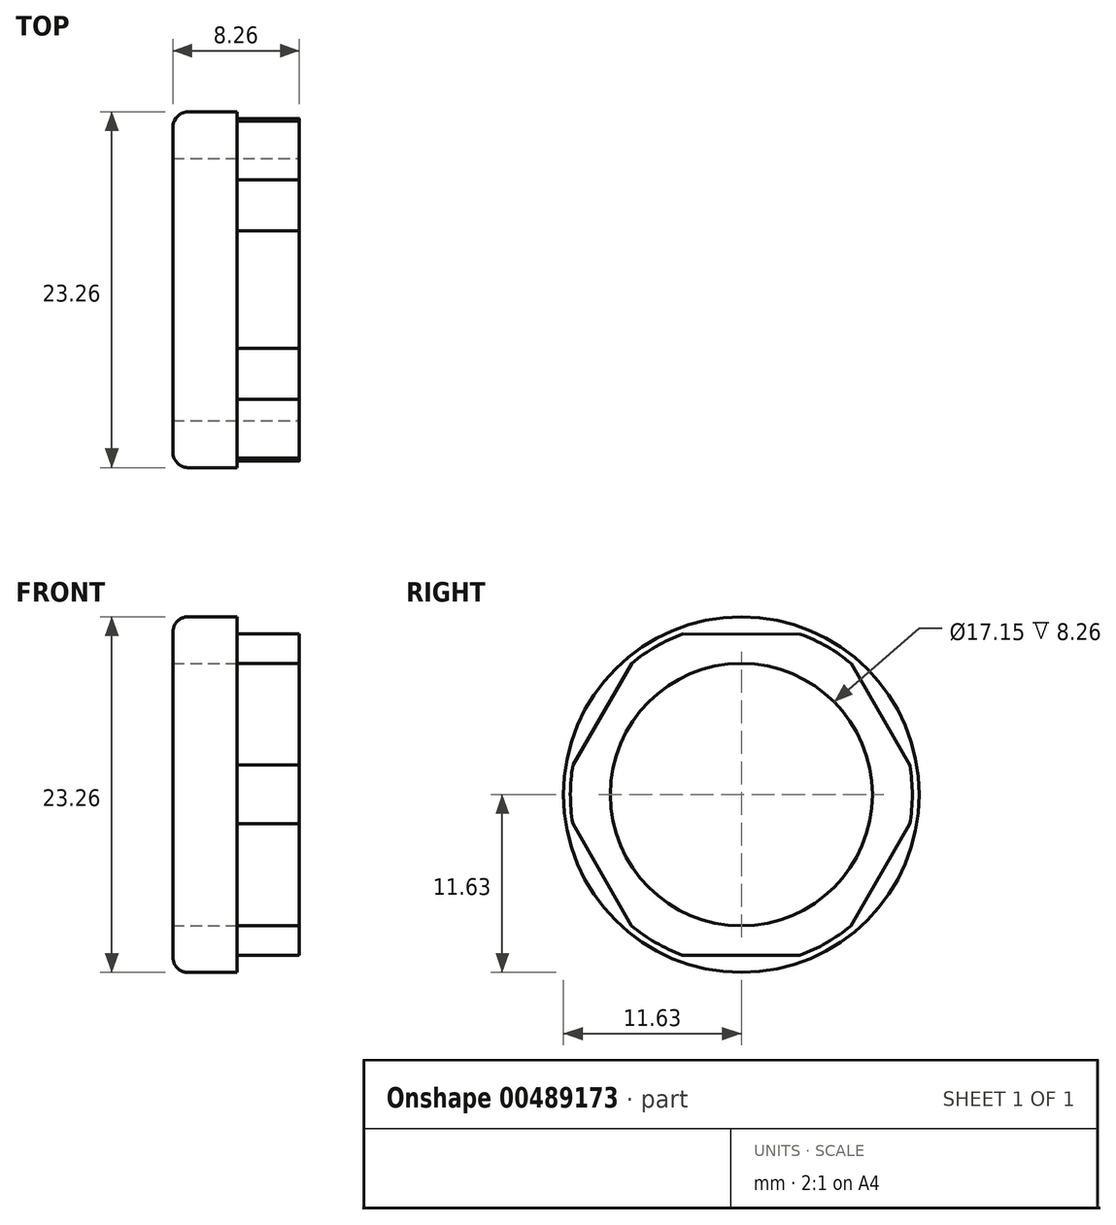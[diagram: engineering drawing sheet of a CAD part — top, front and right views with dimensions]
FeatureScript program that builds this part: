
annotation { "Feature Type Name" : "Feature", "Feature Type Description" : "" }
export const myFeature = defineFeature(function(context is Context, id is Id, definition is map)
    precondition{}
    {
        {
            var Q0;
            Q0=qCreatedBy(makeId("Front.planeOp"),FACE);
            var sketch = newSketch(context, id + "F0", { "sketchPlane" : qUnion([Q0])});
            skLineSegment(sketch, "E0", {"start": v(4.06, 8.57) * mm, "end": v(-4.2, 8.57) * mm});
            skLineSegment(sketch, "E1", {"start": v(-4.2, 8.57) * mm, "end": v(-4.2, 11.63) * mm});
            skLineSegment(sketch, "E2", {"start": v(-4.2, 11.63) * mm, "end": v(0, 11.63) * mm});
            skLineSegment(sketch, "E3", {"start": v(0, 11.63) * mm, "end": v(0, 11.18) * mm});
            skLineSegment(sketch, "E4", {"start": v(0, 11.18) * mm, "end": v(4.06, 11.18) * mm});
            skLineSegment(sketch, "E5", {"start": v(4.06, 11.18) * mm, "end": v(4.06, 8.57) * mm});
            skLineSegment(sketch, "E6", {"start": v(7.39, 0) * mm, "end": v(-7.21, 0) * mm, "construction": true});
            skSolve(sketch);
        }
        {
            var Q0;
            Q0=makeQuery(id+"F0.imprint","IMPRINT",FACE,{"disambiguationData":[TD([[makeQuery(id+"F0.imprint","IMPRINT",EDGE,{"derivedFrom":sQuery(id+"F0.wireOp",EDGE,"E0")}),-1.0]])]});
            var Q1;
            Q1=sQuery(id+"F0.wireOp",EDGE,"E6");
            revolve(context, id + "F1", {"entities" : qUnion([Q0]), "axis" : qUnion([Q1]), "revolveType" : RevolveType.FULL});
        }
        {
            var Q0;
            Q0=qCreatedBy(makeId("Right.planeOp"),FACE);
            var sketch = newSketch(context, id + "F2", { "sketchPlane" : qUnion([Q0])});
            skCircle(sketch, "E7.cCircle", {"center": v(0, 0) * mm, "radius": 10.5 * mm, "construction": true});
            skLineSegment(sketch, "E7.0", {"start": v(6.08, 10.49) * mm, "end": v(12.12, -0.02) * mm});
            skLineSegment(sketch, "E7.1", {"start": v(12.12, -0.02) * mm, "end": v(6.04, -10.51) * mm});
            skLineSegment(sketch, "E7.2", {"start": v(6.04, -10.51) * mm, "end": v(-6.08, -10.49) * mm});
            skLineSegment(sketch, "E7.3", {"start": v(-6.08, -10.49) * mm, "end": v(-12.12, 0.02) * mm});
            skLineSegment(sketch, "E7.4", {"start": v(-12.12, 0.02) * mm, "end": v(-6.04, 10.51) * mm});
            skLineSegment(sketch, "E7.5", {"start": v(-6.04, 10.51) * mm, "end": v(6.08, 10.49) * mm});
            skPoint(sketch, "E7.0.midPoint", {"position": v(9.1, 5.23) * mm});
            skCircle(sketch, "E8", {"center": v(0, 0) * mm, "radius": 12.5 * mm});
            skSolve(sketch);
        }
        {
            var Q0;
            Q0=makeQuery(id+"F2.imprint","IMPRINT",FACE,{"disambiguationData":[TD([[makeQuery(id+"F2.imprint","IMPRINT",EDGE,{"derivedFrom":sQuery(id+"F2.wireOp",EDGE,"E7.0")}),1.0]])]});
            var Q1;
            Q1=makeQuery(id+"F1.opRevolve","SWEPT_FACE",FACE,{"disambiguationData":[OSD([sQuery(id+"F0.wireOp",EDGE,"E5")])]});
            extrude(context, id + "F3", {"entities" : qUnion([Q0]), "operationType" : NewBodyOperationType.REMOVE, "endBound" : BoundingType.UP_TO_SURFACE, "endBoundEntityFace" : qUnion([Q1]), "depth" : 25 * mm});
        }
        {
            var Q0;
            Q0=makeQuery(id+"F1.opRevolve","SWEPT_EDGE",EDGE,{"disambiguationData":[OSD([sQuery(id+"F0.wireOp",EDGE,"E1"),sQuery(id+"F0.wireOp",EDGE,"E2")])]});
            fillet(context, id + "F4", {"entities" : qUnion([Q0]), "radius" : 1 * mm, "tangentPropagation" : true, "allowEdgeOverflow" : false});
        }
    });
